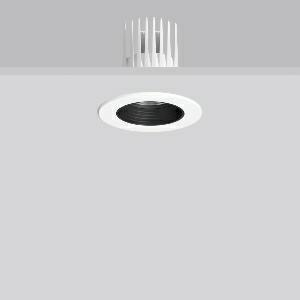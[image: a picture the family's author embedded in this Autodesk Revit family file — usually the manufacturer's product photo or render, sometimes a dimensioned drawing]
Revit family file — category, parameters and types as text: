
# Revit family: heledon_mini_e_901743_002_76_88d2
name_source: partatom
category: Lighting Fixtures
units: mm (PartAtom-declared; Revit-internal decimal feet)

## family parameters
Cut with Voids When Loaded = No
Host = Face
Light Source = No
Part Type = Normal
Room Calculation Point = No
Round Connector Dimension = Use Diameter
Shared = No

## types (1)
- HELEDON mini E (1 x LED Modul 930, 2250 lm, 3000)
    Apparent Load = 20 VA
    Approval mark = CE
    CIE Flux Codes = 99 100 100 100 100
    Color Rendering = 90
    Color Temperature = 3000
    Default Elevation = 1800 mm
    Description = Series: HELEDON mini
Round recessed downlight. Housing: die-cast aluminium, powder-coated. Black plastic ring and recessed LED to prevent glare from the side. Optical assembly with lens made of plastic (polycarbonate) for the best homogeneous light distribution - can be changed without tools. Best colour rendering index Ra>90. Suitable for Recessed ceiling mounting. Installation without tools thanks to spring fastening system. Including separate LED converter with connecting cable 600 mm.High quality converter without flickering and stroboscopic effect. Through-wiring box (5 pole) available as accessory. The following accessories can be mounted without use of tools: interchangeable lenses, decorative glasses, honeycomb louvre, clear and frosted diffusers, white interchangeable plastic ring. 
Colour: traffic white, matt (RAL 9016)
Diameter: 124 mm
Height: 3 mm
Cut-out diameter: 114 mm
Recess height: 170 mm
Luminaire: recess height: 120 mm
Lamp: LED
Socket: without socket
Colour temperature: 3000K
Colour rendering index (CRI): 92
System power: 20 W
Rated luminous flux: 2250 lm
Luminous efficiency: 113 lm/W
Control gear: Converter, dimmable, DALI
Protection class: II
Type of protection: IP 20
    Height = 0 mm  [stored 0 ft]
    Lamp = 1 x LED Modul 930
    Lamp Light Flux = 2250 lm
    Lamp count = 1
    Length = 124 mm
    Lifetime = 50000 h
    Luminous efficacy = 113 lm/W
    Manufacturer = RZB
    ModVariant = No
    Model = 901743.002.76
    Mounting Place = Ceiling
    Mounting Type = Recessed
    Number of Poles = 1
    OnlyDefault = Yes
    Power Factor = 1
    Product Name = HELEDON mini E
    Product group = Recessed downlights
    ProductGroupID = 402
    Protection Class = Protection class II
    Protection Degree = IP 20
    RLX_Detail_Level = 1
    RLX_Emergency_Light_Flux = 0 lm
    RLX_Emergency_Type = 0
    RLX_Emergency_Type_DB = No
    RlxData = <blob elided: 128393 chars, md5=f03134c7>
    Socket = socket
    Standby Power = 0 W
    System Light Flux = 2250 lm
    System Power = 20 W
    Type Comments = Product without accessories
    Type Image = 901656.002.jpg
    URL = http://relux.com
    VarID = ---
    Voltage = 230 V
    Voltage Range = 220-240 V
    Weight = 0.00 kg
    Width = 0 mm  [stored 0 ft]

note: [stored X ft] marks values corroborated as IEEE doubles in the binary element streams (Revit-internal decimal feet)

## geometry (parser evidence)
native form markers: Blend x4, Sweep x11
no freeform markers — native parametric forms only
